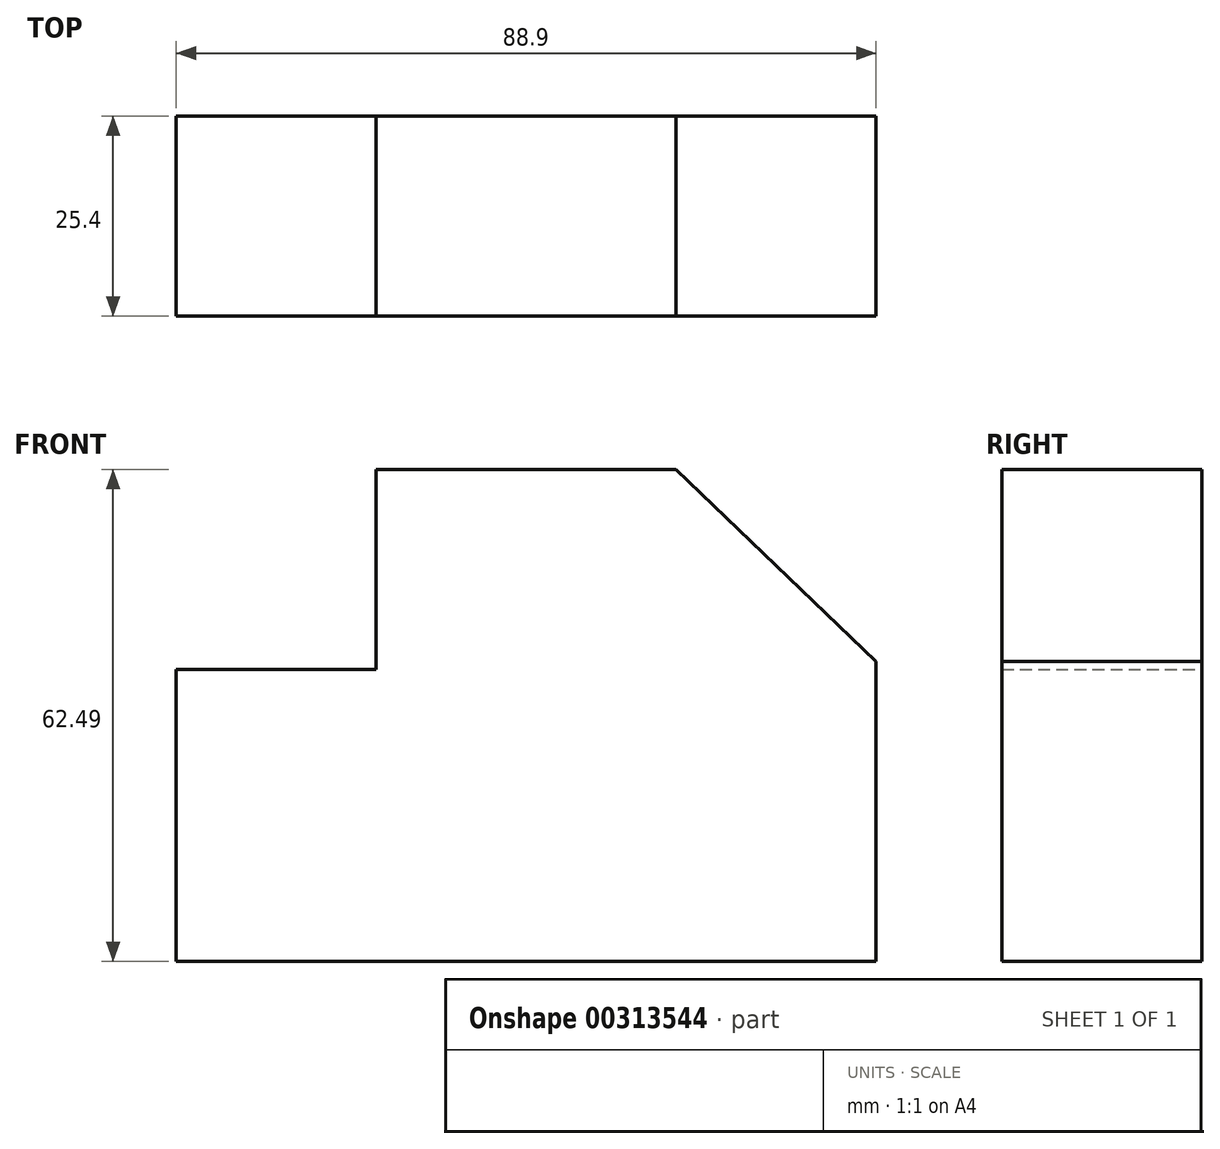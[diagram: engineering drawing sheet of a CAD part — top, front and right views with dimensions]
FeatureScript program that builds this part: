
annotation { "Feature Type Name" : "Feature", "Feature Type Description" : "" }
export const myFeature = defineFeature(function(context is Context, id is Id, definition is map)
    precondition{}
    {
        {
            var Q0;
            Q0=qCreatedBy(makeId("Front.planeOp"),FACE);
            var sketch = newSketch(context, id + "F0", { "sketchPlane" : qUnion([Q0])});
            skLineSegment(sketch, "E0", {"start": v(-48.87, -51.08) * mm, "end": v(40.03, -51.08) * mm});
            skLineSegment(sketch, "E1", {"start": v(40.03, -51.08) * mm, "end": v(40.03, -12.98) * mm});
            skLineSegment(sketch, "E2", {"start": v(40.03, -12.98) * mm, "end": v(14.63, 11.41) * mm});
            skLineSegment(sketch, "E3", {"start": v(14.63, 11.41) * mm, "end": v(-23.47, 11.41) * mm});
            skLineSegment(sketch, "E4", {"start": v(-23.47, 11.41) * mm, "end": v(-23.47, -13.99) * mm});
            skLineSegment(sketch, "E5", {"start": v(-23.47, -13.99) * mm, "end": v(-48.87, -13.99) * mm});
            skLineSegment(sketch, "E6", {"start": v(-48.87, -13.99) * mm, "end": v(-48.87, -51.08) * mm});
            skSolve(sketch);
        }
        {
            var Q0;
            Q0 = qSketchRegion(id + "F0", true);
            extrude(context, id + "F1", {"entities" : qUnion([Q0]), "depth" : 25.4 * mm});
        }
    });
